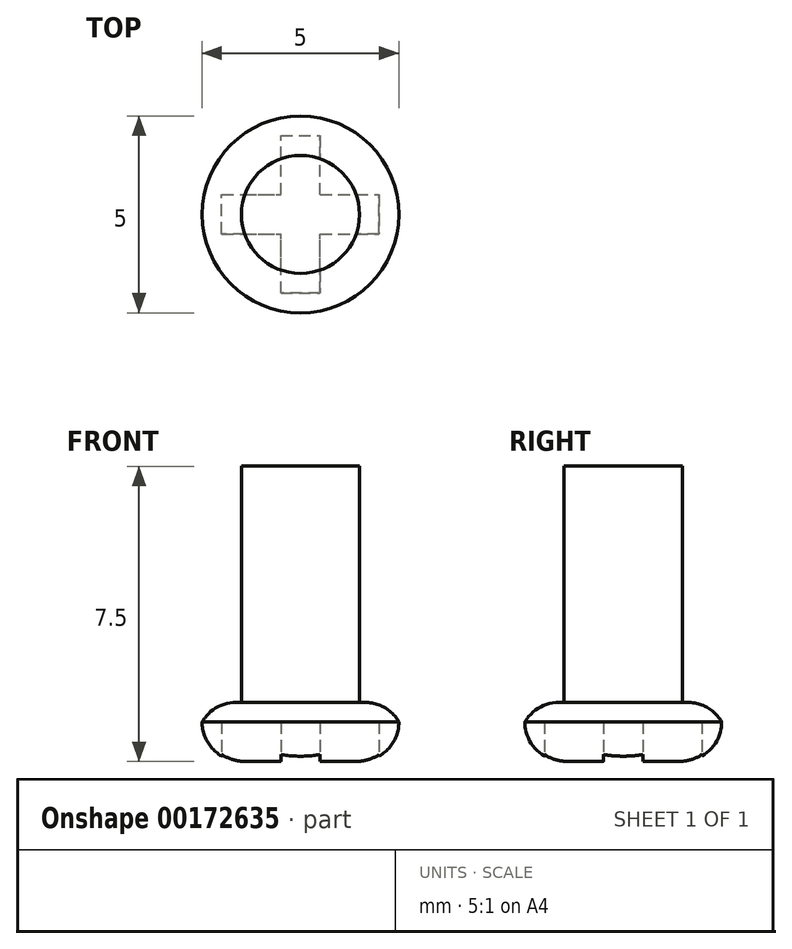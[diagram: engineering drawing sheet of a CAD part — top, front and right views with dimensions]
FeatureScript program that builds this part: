
annotation { "Feature Type Name" : "Feature", "Feature Type Description" : "" }
export const myFeature = defineFeature(function(context is Context, id is Id, definition is map)
    precondition{}
    {
        {
            var Q0;
            Q0=qCreatedBy(makeId("Top.planeOp"),FACE);
            var sketch = newSketch(context, id + "F0", { "sketchPlane" : qUnion([Q0])});
            skCircle(sketch, "E0", {"center": v(0, 0) * mm, "radius": 1.5 * mm});
            skSolve(sketch);
        }
        {
            var Q0;
            Q0=qSketchRegion(id+"F0",true);
            extrude(context, id + "F1", {"entities" : qUnion([Q0]), "depth" : 6 * mm});
        }
        {
            var Q0;
            Q0=makeQuery(id+"F1.opExtrude","CAP_FACE",FACE,{"disambiguationData":[OSD([sQuery(id+"F0.wireOp",EDGE,"E0")])],"isStart":false});
            var sketch = newSketch(context, id + "F2", { "sketchPlane" : qUnion([Q0])});
            skCircle(sketch, "E1", {"center": v(0, 0) * mm, "radius": 2.5 * mm});
            skSolve(sketch);
        }
        {
            var Q0;
            Q0=qSketchRegion(id+"F2",true);
            extrude(context, id + "F3", {"entities" : qUnion([Q0]), "operationType" : NewBodyOperationType.ADD, "depth" : 1.5 * mm});
        }
        {
            var Q0;
            Q0=makeQuery(id+"F3.opExtrude","CAP_FACE",FACE,{"disambiguationData":[OSD([sQuery(id+"F2.wireOp",EDGE,"E1")])],"isStart":false});
            var sketch = newSketch(context, id + "F4", { "sketchPlane" : qUnion([Q0])});
            skLineSegment(sketch, "E2.bottom", {"start": v(-0.5, 2) * mm, "end": v(0.5, 2) * mm});
            skLineSegment(sketch, "E2.top", {"start": v(-0.5, -2) * mm, "end": v(0.5, -2) * mm});
            skLineSegment(sketch, "E2.left", {"start": v(-0.5, 2) * mm, "end": v(-0.5, -2) * mm});
            skLineSegment(sketch, "E2.right", {"start": v(0.5, 2) * mm, "end": v(0.5, -2) * mm});
            skPoint(sketch, "E2.middle", {"position": v(0, 0) * mm});
            skLineSegment(sketch, "E3.bottom", {"start": v(-2, 0.5) * mm, "end": v(2, 0.5) * mm});
            skLineSegment(sketch, "E3.top", {"start": v(-2, -0.5) * mm, "end": v(2, -0.5) * mm});
            skLineSegment(sketch, "E3.left", {"start": v(-2, 0.5) * mm, "end": v(-2, -0.5) * mm});
            skLineSegment(sketch, "E3.right", {"start": v(2, 0.5) * mm, "end": v(2, -0.5) * mm});
            skSolve(sketch);
        }
        {
            var Q0;
            Q0=qSketchRegion(id+"F4",true);
            extrude(context, id + "F5", {"entities" : qUnion([Q0]), "operationType" : NewBodyOperationType.REMOVE, "oppositeDirection" : true, "depth" : 1 * mm});
        }
        {
            var Q0;
            Q0=makeQuery(id+"F3.opExtrude","CAP_EDGE",EDGE,{"disambiguationData":[OSD([sQuery(id+"F2.wireOp",EDGE,"E1")])],"isStart":false});
            fillet(context, id + "F6", {"entities" : qUnion([Q0]), "radius" : 1 * mm, "tangentPropagation" : true, "allowEdgeOverflow" : false});
        }
        {
            var Q0;
            Q0=makeQuery(id+"F3.opExtrude","CAP_EDGE",EDGE,{"disambiguationData":[OSD([sQuery(id+"F2.wireOp",EDGE,"E1")])],"isStart":true});
            fillet(context, id + "F7", {"entities" : qUnion([Q0]), "radius" : 1 * mm, "tangentPropagation" : true, "allowEdgeOverflow" : false});
        }
        {
            var Q0;
            Q0=qCreatedBy(makeId("Front.planeOp"),FACE);
            var sketch = newSketch(context, id + "F8", { "sketchPlane" : qUnion([Q0])});
            skLineSegment(sketch, "E4", {"start": v(0, 0) * mm, "end": v(3.56, 0) * mm});
            skSolve(sketch);
        }
        {
            var Q0;
            Q0=makeQuery(id+"F1.opExtrude","SWEPT_BODY",BODY,{"disambiguationData":[OSD([sQuery(id+"F0.wireOp",EDGE,"E0")])]});
            var Q1;
            Q1=sQuery(id+"F8.wireOp",EDGE,"E4");
            transform(context, id + "F9", {"entities" : qUnion([Q0]), "transformType" : TransformType.ROTATION, "transformAxis" : qUnion([Q1]), "angle" : 180 * degree, "makeCopy" : false});
        }
    });
